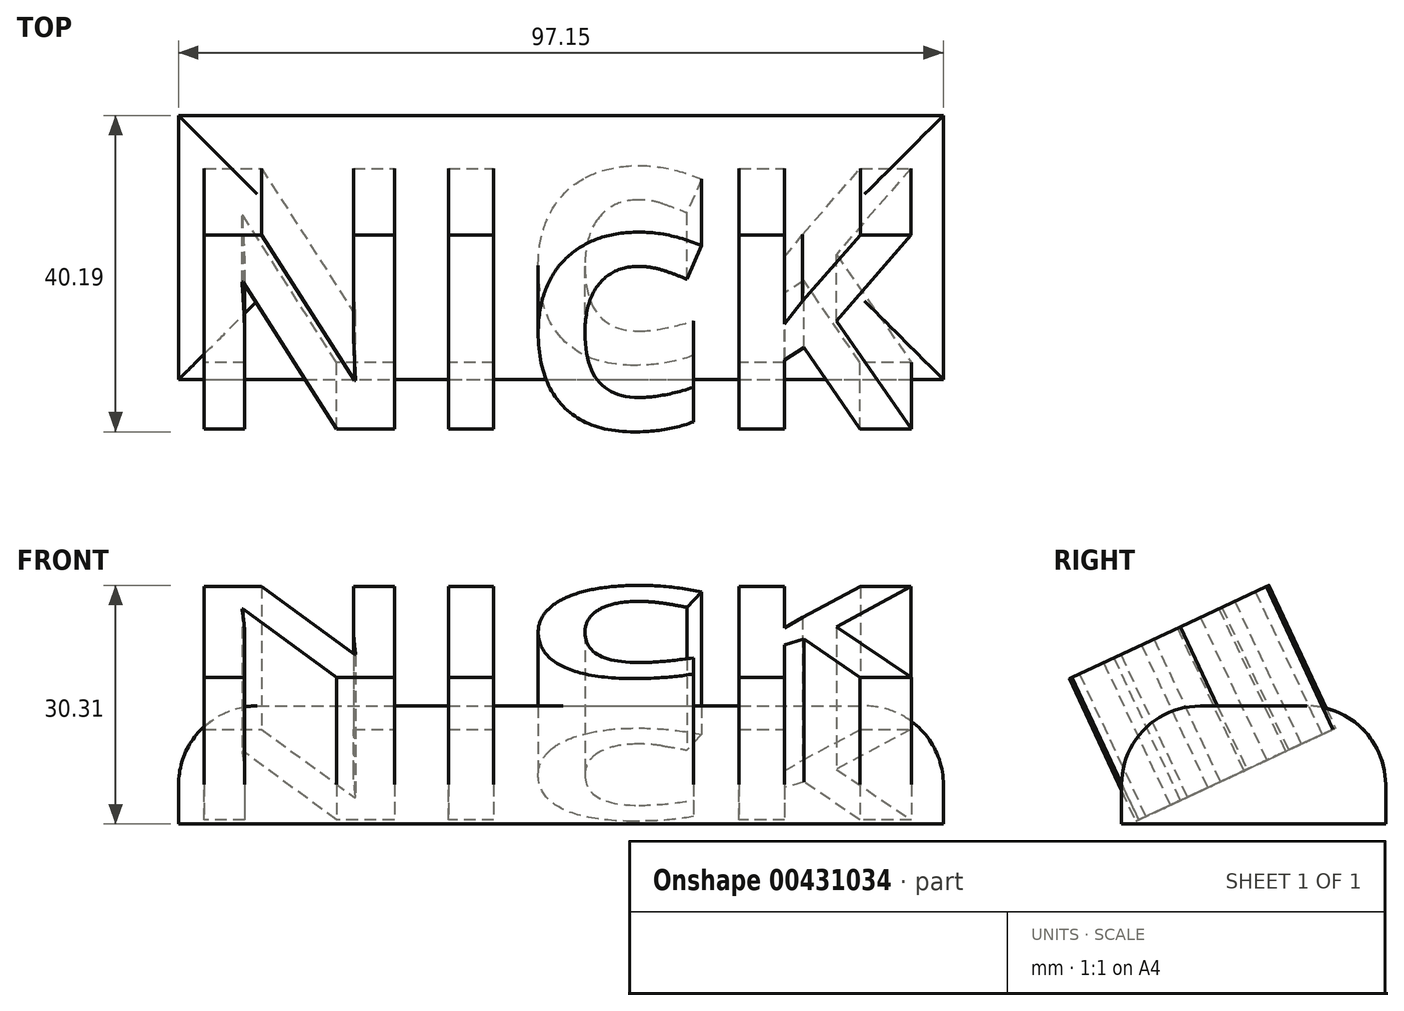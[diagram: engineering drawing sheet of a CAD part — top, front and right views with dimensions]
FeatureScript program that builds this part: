
annotation { "Feature Type Name" : "Feature", "Feature Type Description" : "" }
export const myFeature = defineFeature(function(context is Context, id is Id, definition is map)
    precondition{}
    {
        {
            var Q0;
            Q0=qCreatedBy(makeId("Top.planeOp"),FACE);
            var sketch = newSketch(context, id + "F0", { "sketchPlane" : qUnion([Q0])});
            skText(sketch, "E0", { "text": "NICK", "fontName": "OpenSans-Bold.ttf"});
            const initialGuessF0  = {"E0": [-0.04957, -0.04822, 1, 0, 0.02747]};
            skSetInitialGuess(sketch, initialGuessF0);
            skSolve(sketch);
        }
        {
            var Q0;
            Q0=makeQuery(id+"F0.imprint","IMPRINT",FACE,{"disambiguationData":[TD([[makeQuery(id+"F0.imprint","IMPRINT",EDGE,{"derivedFrom":sQuery(id+"F0.wireOp",EDGE,"E0.sketch_text.stroke-0")}),-1.0]])]});
            var Q1;
            Q1=makeQuery(id+"F0.imprint","IMPRINT",FACE,{"disambiguationData":[TD([[makeQuery(id+"F0.imprint","IMPRINT",EDGE,{"derivedFrom":sQuery(id+"F0.wireOp",EDGE,"E0.sketch_text.stroke-14")}),-1.0]])]});
            var Q2;
            Q2=makeQuery(id+"F0.imprint","IMPRINT",FACE,{"disambiguationData":[TD([[makeQuery(id+"F0.imprint","IMPRINT",EDGE,{"derivedFrom":sQuery(id+"F0.wireOp",EDGE,"E0.sketch_text.stroke-18")}),-1.0]])]});
            var Q3;
            Q3=makeQuery(id+"F0.imprint","IMPRINT",FACE,{"disambiguationData":[TD([[makeQuery(id+"F0.imprint","IMPRINT",EDGE,{"derivedFrom":sQuery(id+"F0.wireOp",EDGE,"E0.sketch_text.stroke-33")}),-1.0]])]});
            extrude(context, id + "F1", {"entities" : qUnion([Q0, Q1, Q2, Q3]), "depth" : 20 * mm});
        }
        {
            var Q0;
            Q0=makeQuery(id+"F1.opExtrude","SWEPT_BODY",BODY,{"disambiguationData":[OSD([sQuery(id+"F0.wireOp",EDGE,"E0.sketch_text.stroke-0"),sQuery(id+"F0.wireOp",EDGE,"E0.sketch_text.stroke-1"),sQuery(id+"F0.wireOp",EDGE,"E0.sketch_text.stroke-2"),sQuery(id+"F0.wireOp",EDGE,"E0.sketch_text.stroke-3"),sQuery(id+"F0.wireOp",EDGE,"E0.sketch_text.stroke-4"),sQuery(id+"F0.wireOp",EDGE,"E0.sketch_text.stroke-5"),sQuery(id+"F0.wireOp",EDGE,"E0.sketch_text.stroke-6"),sQuery(id+"F0.wireOp",EDGE,"E0.sketch_text.stroke-7"),sQuery(id+"F0.wireOp",EDGE,"E0.sketch_text.stroke-8"),sQuery(id+"F0.wireOp",EDGE,"E0.sketch_text.stroke-9"),sQuery(id+"F0.wireOp",EDGE,"E0.sketch_text.stroke-10"),sQuery(id+"F0.wireOp",EDGE,"E0.sketch_text.stroke-11"),sQuery(id+"F0.wireOp",EDGE,"E0.sketch_text.stroke-12"),sQuery(id+"F0.wireOp",EDGE,"E0.sketch_text.stroke-13")])]});
            var Q1;
            Q1=makeQuery(id+"F1.opExtrude","SWEPT_BODY",BODY,{"disambiguationData":[OSD([sQuery(id+"F0.wireOp",EDGE,"E0.sketch_text.stroke-14"),sQuery(id+"F0.wireOp",EDGE,"E0.sketch_text.stroke-15"),sQuery(id+"F0.wireOp",EDGE,"E0.sketch_text.stroke-16"),sQuery(id+"F0.wireOp",EDGE,"E0.sketch_text.stroke-17")])]});
            var Q2;
            Q2=makeQuery(id+"F1.opExtrude","SWEPT_BODY",BODY,{"disambiguationData":[OSD([sQuery(id+"F0.wireOp",EDGE,"E0.sketch_text.stroke-18"),sQuery(id+"F0.wireOp",EDGE,"E0.sketch_text.stroke-19"),sQuery(id+"F0.wireOp",EDGE,"E0.sketch_text.stroke-20"),sQuery(id+"F0.wireOp",EDGE,"E0.sketch_text.stroke-21"),sQuery(id+"F0.wireOp",EDGE,"E0.sketch_text.stroke-22"),sQuery(id+"F0.wireOp",EDGE,"E0.sketch_text.stroke-23"),sQuery(id+"F0.wireOp",EDGE,"E0.sketch_text.stroke-24"),sQuery(id+"F0.wireOp",EDGE,"E0.sketch_text.stroke-25"),sQuery(id+"F0.wireOp",EDGE,"E0.sketch_text.stroke-26"),sQuery(id+"F0.wireOp",EDGE,"E0.sketch_text.stroke-27"),sQuery(id+"F0.wireOp",EDGE,"E0.sketch_text.stroke-28"),sQuery(id+"F0.wireOp",EDGE,"E0.sketch_text.stroke-29"),sQuery(id+"F0.wireOp",EDGE,"E0.sketch_text.stroke-30"),sQuery(id+"F0.wireOp",EDGE,"E0.sketch_text.stroke-31"),sQuery(id+"F0.wireOp",EDGE,"E0.sketch_text.stroke-32")])]});
            var Q3;
            Q3=makeQuery(id+"F1.opExtrude","SWEPT_BODY",BODY,{"disambiguationData":[OSD([sQuery(id+"F0.wireOp",EDGE,"E0.sketch_text.stroke-33"),sQuery(id+"F0.wireOp",EDGE,"E0.sketch_text.stroke-34"),sQuery(id+"F0.wireOp",EDGE,"E0.sketch_text.stroke-35"),sQuery(id+"F0.wireOp",EDGE,"E0.sketch_text.stroke-36"),sQuery(id+"F0.wireOp",EDGE,"E0.sketch_text.stroke-37"),sQuery(id+"F0.wireOp",EDGE,"E0.sketch_text.stroke-38"),sQuery(id+"F0.wireOp",EDGE,"E0.sketch_text.stroke-39"),sQuery(id+"F0.wireOp",EDGE,"E0.sketch_text.stroke-40"),sQuery(id+"F0.wireOp",EDGE,"E0.sketch_text.stroke-41"),sQuery(id+"F0.wireOp",EDGE,"E0.sketch_text.stroke-42"),sQuery(id+"F0.wireOp",EDGE,"E0.sketch_text.stroke-43"),sQuery(id+"F0.wireOp",EDGE,"E0.sketch_text.stroke-44"),sQuery(id+"F0.wireOp",EDGE,"E0.sketch_text.stroke-45")])]});
            var Q4;
            Q4=makeQuery(id+"F1.opExtrude","CAP_EDGE",EDGE,{"disambiguationData":[OSD([sQuery(id+"F0.wireOp",EDGE,"E0.sketch_text.stroke-17")])],"isStart":true});
            transform(context, id + "F2", {"entities" : qUnion([Q0, Q1, Q2, Q3]), "transformType" : TransformType.ROTATION, "transformAxis" : qUnion([Q4]), "angle" : 45 * degree, "oppositeDirection" : true, "makeCopy" : false});
        }
        {
            var Q0;
            Q0=qCreatedBy(makeId("Top.planeOp"),FACE);
            var sketch = newSketch(context, id + "F3", { "sketchPlane" : qUnion([Q0])});
            skLineSegment(sketch, "E1.bottom", {"start": v(-44.06, 21.02) * mm, "end": v(53.1, 21.02) * mm});
            skLineSegment(sketch, "E1.top", {"start": v(-44.06, -12.54) * mm, "end": v(53.1, -12.54) * mm});
            skLineSegment(sketch, "E1.left", {"start": v(-44.06, 21.02) * mm, "end": v(-44.06, -12.54) * mm});
            skLineSegment(sketch, "E1.right", {"start": v(53.1, 21.02) * mm, "end": v(53.1, -12.54) * mm});
            skSolve(sketch);
        }
        {
            var Q0;
            Q0=makeQuery(id+"F3.imprint","IMPRINT",FACE,{"disambiguationData":[TD([[makeQuery(id+"F3.imprint","IMPRINT",EDGE,{"derivedFrom":sQuery(id+"F3.wireOp",EDGE,"E1.bottom")}),-1.0]])]});
            extrude(context, id + "F4", {"entities" : qUnion([Q0]), "depth" : 15 * mm});
        }
        {
            var Q0;
            Q0=makeQuery(id+"F4.opExtrude","CAP_EDGE",EDGE,{"disambiguationData":[OSD([sQuery(id+"F3.wireOp",EDGE,"E1.left")])],"isStart":false});
            var Q1;
            Q1=makeQuery(id+"F4.opExtrude","CAP_EDGE",EDGE,{"disambiguationData":[OSD([sQuery(id+"F3.wireOp",EDGE,"E1.bottom")])],"isStart":false});
            var Q2;
            Q2=makeQuery(id+"F4.opExtrude","CAP_EDGE",EDGE,{"disambiguationData":[OSD([sQuery(id+"F3.wireOp",EDGE,"E1.right")])],"isStart":false});
            var Q3;
            Q3=makeQuery(id+"F4.opExtrude","CAP_EDGE",EDGE,{"disambiguationData":[OSD([sQuery(id+"F3.wireOp",EDGE,"E1.top")])],"isStart":false});
            fillet(context, id + "F5", {"entities" : qUnion([Q0, Q1, Q2, Q3]), "radius" : 10 * mm, "tangentPropagation" : true, "allowEdgeOverflow" : false});
        }
        {
            var Q0;
            Q0=makeQuery(id+"F1.opExtrude","SWEPT_BODY",BODY,{"disambiguationData":[OSD([sQuery(id+"F0.wireOp",EDGE,"E0.sketch_text.stroke-0"),sQuery(id+"F0.wireOp",EDGE,"E0.sketch_text.stroke-1"),sQuery(id+"F0.wireOp",EDGE,"E0.sketch_text.stroke-2"),sQuery(id+"F0.wireOp",EDGE,"E0.sketch_text.stroke-3"),sQuery(id+"F0.wireOp",EDGE,"E0.sketch_text.stroke-4"),sQuery(id+"F0.wireOp",EDGE,"E0.sketch_text.stroke-5"),sQuery(id+"F0.wireOp",EDGE,"E0.sketch_text.stroke-6"),sQuery(id+"F0.wireOp",EDGE,"E0.sketch_text.stroke-7"),sQuery(id+"F0.wireOp",EDGE,"E0.sketch_text.stroke-8"),sQuery(id+"F0.wireOp",EDGE,"E0.sketch_text.stroke-9"),sQuery(id+"F0.wireOp",EDGE,"E0.sketch_text.stroke-10"),sQuery(id+"F0.wireOp",EDGE,"E0.sketch_text.stroke-11"),sQuery(id+"F0.wireOp",EDGE,"E0.sketch_text.stroke-12"),sQuery(id+"F0.wireOp",EDGE,"E0.sketch_text.stroke-13")])]});
            var Q1;
            Q1=makeQuery(id+"F1.opExtrude","SWEPT_BODY",BODY,{"disambiguationData":[OSD([sQuery(id+"F0.wireOp",EDGE,"E0.sketch_text.stroke-14"),sQuery(id+"F0.wireOp",EDGE,"E0.sketch_text.stroke-15"),sQuery(id+"F0.wireOp",EDGE,"E0.sketch_text.stroke-16"),sQuery(id+"F0.wireOp",EDGE,"E0.sketch_text.stroke-17")])]});
            var Q2;
            Q2=makeQuery(id+"F1.opExtrude","SWEPT_BODY",BODY,{"disambiguationData":[OSD([sQuery(id+"F0.wireOp",EDGE,"E0.sketch_text.stroke-18"),sQuery(id+"F0.wireOp",EDGE,"E0.sketch_text.stroke-19"),sQuery(id+"F0.wireOp",EDGE,"E0.sketch_text.stroke-20"),sQuery(id+"F0.wireOp",EDGE,"E0.sketch_text.stroke-21"),sQuery(id+"F0.wireOp",EDGE,"E0.sketch_text.stroke-22"),sQuery(id+"F0.wireOp",EDGE,"E0.sketch_text.stroke-23"),sQuery(id+"F0.wireOp",EDGE,"E0.sketch_text.stroke-24"),sQuery(id+"F0.wireOp",EDGE,"E0.sketch_text.stroke-25"),sQuery(id+"F0.wireOp",EDGE,"E0.sketch_text.stroke-26"),sQuery(id+"F0.wireOp",EDGE,"E0.sketch_text.stroke-27"),sQuery(id+"F0.wireOp",EDGE,"E0.sketch_text.stroke-28"),sQuery(id+"F0.wireOp",EDGE,"E0.sketch_text.stroke-29"),sQuery(id+"F0.wireOp",EDGE,"E0.sketch_text.stroke-30"),sQuery(id+"F0.wireOp",EDGE,"E0.sketch_text.stroke-31"),sQuery(id+"F0.wireOp",EDGE,"E0.sketch_text.stroke-32")])]});
            var Q3;
            Q3=makeQuery(id+"F1.opExtrude","SWEPT_BODY",BODY,{"disambiguationData":[OSD([sQuery(id+"F0.wireOp",EDGE,"E0.sketch_text.stroke-33"),sQuery(id+"F0.wireOp",EDGE,"E0.sketch_text.stroke-34"),sQuery(id+"F0.wireOp",EDGE,"E0.sketch_text.stroke-35"),sQuery(id+"F0.wireOp",EDGE,"E0.sketch_text.stroke-36"),sQuery(id+"F0.wireOp",EDGE,"E0.sketch_text.stroke-37"),sQuery(id+"F0.wireOp",EDGE,"E0.sketch_text.stroke-38"),sQuery(id+"F0.wireOp",EDGE,"E0.sketch_text.stroke-39"),sQuery(id+"F0.wireOp",EDGE,"E0.sketch_text.stroke-40"),sQuery(id+"F0.wireOp",EDGE,"E0.sketch_text.stroke-41"),sQuery(id+"F0.wireOp",EDGE,"E0.sketch_text.stroke-42"),sQuery(id+"F0.wireOp",EDGE,"E0.sketch_text.stroke-43"),sQuery(id+"F0.wireOp",EDGE,"E0.sketch_text.stroke-44"),sQuery(id+"F0.wireOp",EDGE,"E0.sketch_text.stroke-45")])]});
            transform(context, id + "F6", {"entities" : qUnion([Q0, Q1, Q2, Q3]), "transformType" : TransformType.TRANSLATION_3D, "dx" : 5.33 * mm, "dy" : 37.85 * mm, "dz" : 0 * mm, "makeCopy" : false});
        }
        {
            var Q0;
            Q0=makeQuery(id+"F1.opExtrude","SWEPT_BODY",BODY,{"disambiguationData":[OSD([sQuery(id+"F0.wireOp",EDGE,"E0.sketch_text.stroke-0"),sQuery(id+"F0.wireOp",EDGE,"E0.sketch_text.stroke-1"),sQuery(id+"F0.wireOp",EDGE,"E0.sketch_text.stroke-2"),sQuery(id+"F0.wireOp",EDGE,"E0.sketch_text.stroke-3"),sQuery(id+"F0.wireOp",EDGE,"E0.sketch_text.stroke-4"),sQuery(id+"F0.wireOp",EDGE,"E0.sketch_text.stroke-5"),sQuery(id+"F0.wireOp",EDGE,"E0.sketch_text.stroke-6"),sQuery(id+"F0.wireOp",EDGE,"E0.sketch_text.stroke-7"),sQuery(id+"F0.wireOp",EDGE,"E0.sketch_text.stroke-8"),sQuery(id+"F0.wireOp",EDGE,"E0.sketch_text.stroke-9"),sQuery(id+"F0.wireOp",EDGE,"E0.sketch_text.stroke-10"),sQuery(id+"F0.wireOp",EDGE,"E0.sketch_text.stroke-11"),sQuery(id+"F0.wireOp",EDGE,"E0.sketch_text.stroke-12"),sQuery(id+"F0.wireOp",EDGE,"E0.sketch_text.stroke-13")])]});
            var Q1;
            Q1=makeQuery(id+"F1.opExtrude","SWEPT_BODY",BODY,{"disambiguationData":[OSD([sQuery(id+"F0.wireOp",EDGE,"E0.sketch_text.stroke-14"),sQuery(id+"F0.wireOp",EDGE,"E0.sketch_text.stroke-15"),sQuery(id+"F0.wireOp",EDGE,"E0.sketch_text.stroke-16"),sQuery(id+"F0.wireOp",EDGE,"E0.sketch_text.stroke-17")])]});
            var Q2;
            Q2=makeQuery(id+"F1.opExtrude","SWEPT_BODY",BODY,{"disambiguationData":[OSD([sQuery(id+"F0.wireOp",EDGE,"E0.sketch_text.stroke-18"),sQuery(id+"F0.wireOp",EDGE,"E0.sketch_text.stroke-19"),sQuery(id+"F0.wireOp",EDGE,"E0.sketch_text.stroke-20"),sQuery(id+"F0.wireOp",EDGE,"E0.sketch_text.stroke-21"),sQuery(id+"F0.wireOp",EDGE,"E0.sketch_text.stroke-22"),sQuery(id+"F0.wireOp",EDGE,"E0.sketch_text.stroke-23"),sQuery(id+"F0.wireOp",EDGE,"E0.sketch_text.stroke-24"),sQuery(id+"F0.wireOp",EDGE,"E0.sketch_text.stroke-25"),sQuery(id+"F0.wireOp",EDGE,"E0.sketch_text.stroke-26"),sQuery(id+"F0.wireOp",EDGE,"E0.sketch_text.stroke-27"),sQuery(id+"F0.wireOp",EDGE,"E0.sketch_text.stroke-28"),sQuery(id+"F0.wireOp",EDGE,"E0.sketch_text.stroke-29"),sQuery(id+"F0.wireOp",EDGE,"E0.sketch_text.stroke-30"),sQuery(id+"F0.wireOp",EDGE,"E0.sketch_text.stroke-31"),sQuery(id+"F0.wireOp",EDGE,"E0.sketch_text.stroke-32")])]});
            var Q3;
            Q3=makeQuery(id+"F1.opExtrude","SWEPT_BODY",BODY,{"disambiguationData":[OSD([sQuery(id+"F0.wireOp",EDGE,"E0.sketch_text.stroke-33"),sQuery(id+"F0.wireOp",EDGE,"E0.sketch_text.stroke-34"),sQuery(id+"F0.wireOp",EDGE,"E0.sketch_text.stroke-35"),sQuery(id+"F0.wireOp",EDGE,"E0.sketch_text.stroke-36"),sQuery(id+"F0.wireOp",EDGE,"E0.sketch_text.stroke-37"),sQuery(id+"F0.wireOp",EDGE,"E0.sketch_text.stroke-38"),sQuery(id+"F0.wireOp",EDGE,"E0.sketch_text.stroke-39"),sQuery(id+"F0.wireOp",EDGE,"E0.sketch_text.stroke-40"),sQuery(id+"F0.wireOp",EDGE,"E0.sketch_text.stroke-41"),sQuery(id+"F0.wireOp",EDGE,"E0.sketch_text.stroke-42"),sQuery(id+"F0.wireOp",EDGE,"E0.sketch_text.stroke-43"),sQuery(id+"F0.wireOp",EDGE,"E0.sketch_text.stroke-44"),sQuery(id+"F0.wireOp",EDGE,"E0.sketch_text.stroke-45")])]});
            var Q4;
            Q4=makeQuery(id+"F1.opExtrude","CAP_EDGE",EDGE,{"disambiguationData":[OSD([sQuery(id+"F0.wireOp",EDGE,"E0.sketch_text.stroke-0")])],"isStart":true});
            transform(context, id + "F7", {"entities" : qUnion([Q0, Q1, Q2, Q3]), "transformType" : TransformType.ROTATION, "transformAxis" : qUnion([Q4]), "angle" : 20 * degree, "makeCopy" : false});
        }
        {
            var Q0;
            Q0=makeQuery(id+"F1.opExtrude","SWEPT_BODY",BODY,{"disambiguationData":[OSD([sQuery(id+"F0.wireOp",EDGE,"E0.sketch_text.stroke-0"),sQuery(id+"F0.wireOp",EDGE,"E0.sketch_text.stroke-1"),sQuery(id+"F0.wireOp",EDGE,"E0.sketch_text.stroke-2"),sQuery(id+"F0.wireOp",EDGE,"E0.sketch_text.stroke-3"),sQuery(id+"F0.wireOp",EDGE,"E0.sketch_text.stroke-4"),sQuery(id+"F0.wireOp",EDGE,"E0.sketch_text.stroke-5"),sQuery(id+"F0.wireOp",EDGE,"E0.sketch_text.stroke-6"),sQuery(id+"F0.wireOp",EDGE,"E0.sketch_text.stroke-7"),sQuery(id+"F0.wireOp",EDGE,"E0.sketch_text.stroke-8"),sQuery(id+"F0.wireOp",EDGE,"E0.sketch_text.stroke-9"),sQuery(id+"F0.wireOp",EDGE,"E0.sketch_text.stroke-10"),sQuery(id+"F0.wireOp",EDGE,"E0.sketch_text.stroke-11"),sQuery(id+"F0.wireOp",EDGE,"E0.sketch_text.stroke-12"),sQuery(id+"F0.wireOp",EDGE,"E0.sketch_text.stroke-13")])]});
            var Q1;
            Q1=makeQuery(id+"F1.opExtrude","SWEPT_BODY",BODY,{"disambiguationData":[OSD([sQuery(id+"F0.wireOp",EDGE,"E0.sketch_text.stroke-14"),sQuery(id+"F0.wireOp",EDGE,"E0.sketch_text.stroke-15"),sQuery(id+"F0.wireOp",EDGE,"E0.sketch_text.stroke-16"),sQuery(id+"F0.wireOp",EDGE,"E0.sketch_text.stroke-17")])]});
            var Q2;
            Q2=makeQuery(id+"F1.opExtrude","SWEPT_BODY",BODY,{"disambiguationData":[OSD([sQuery(id+"F0.wireOp",EDGE,"E0.sketch_text.stroke-18"),sQuery(id+"F0.wireOp",EDGE,"E0.sketch_text.stroke-19"),sQuery(id+"F0.wireOp",EDGE,"E0.sketch_text.stroke-20"),sQuery(id+"F0.wireOp",EDGE,"E0.sketch_text.stroke-21"),sQuery(id+"F0.wireOp",EDGE,"E0.sketch_text.stroke-22"),sQuery(id+"F0.wireOp",EDGE,"E0.sketch_text.stroke-23"),sQuery(id+"F0.wireOp",EDGE,"E0.sketch_text.stroke-24"),sQuery(id+"F0.wireOp",EDGE,"E0.sketch_text.stroke-25"),sQuery(id+"F0.wireOp",EDGE,"E0.sketch_text.stroke-26"),sQuery(id+"F0.wireOp",EDGE,"E0.sketch_text.stroke-27"),sQuery(id+"F0.wireOp",EDGE,"E0.sketch_text.stroke-28"),sQuery(id+"F0.wireOp",EDGE,"E0.sketch_text.stroke-29"),sQuery(id+"F0.wireOp",EDGE,"E0.sketch_text.stroke-30"),sQuery(id+"F0.wireOp",EDGE,"E0.sketch_text.stroke-31"),sQuery(id+"F0.wireOp",EDGE,"E0.sketch_text.stroke-32")])]});
            var Q3;
            Q3=makeQuery(id+"F1.opExtrude","SWEPT_BODY",BODY,{"disambiguationData":[OSD([sQuery(id+"F0.wireOp",EDGE,"E0.sketch_text.stroke-33"),sQuery(id+"F0.wireOp",EDGE,"E0.sketch_text.stroke-34"),sQuery(id+"F0.wireOp",EDGE,"E0.sketch_text.stroke-35"),sQuery(id+"F0.wireOp",EDGE,"E0.sketch_text.stroke-36"),sQuery(id+"F0.wireOp",EDGE,"E0.sketch_text.stroke-37"),sQuery(id+"F0.wireOp",EDGE,"E0.sketch_text.stroke-38"),sQuery(id+"F0.wireOp",EDGE,"E0.sketch_text.stroke-39"),sQuery(id+"F0.wireOp",EDGE,"E0.sketch_text.stroke-40"),sQuery(id+"F0.wireOp",EDGE,"E0.sketch_text.stroke-41"),sQuery(id+"F0.wireOp",EDGE,"E0.sketch_text.stroke-42"),sQuery(id+"F0.wireOp",EDGE,"E0.sketch_text.stroke-43"),sQuery(id+"F0.wireOp",EDGE,"E0.sketch_text.stroke-44"),sQuery(id+"F0.wireOp",EDGE,"E0.sketch_text.stroke-45")])]});
            transform(context, id + "F8", {"entities" : qUnion([Q0, Q1, Q2, Q3]), "transformType" : TransformType.TRANSLATION_3D, "dx" : 0 * mm, "dy" : 0 * mm, "dz" : 0.5 * mm, "makeCopy" : false});
        }
    });
